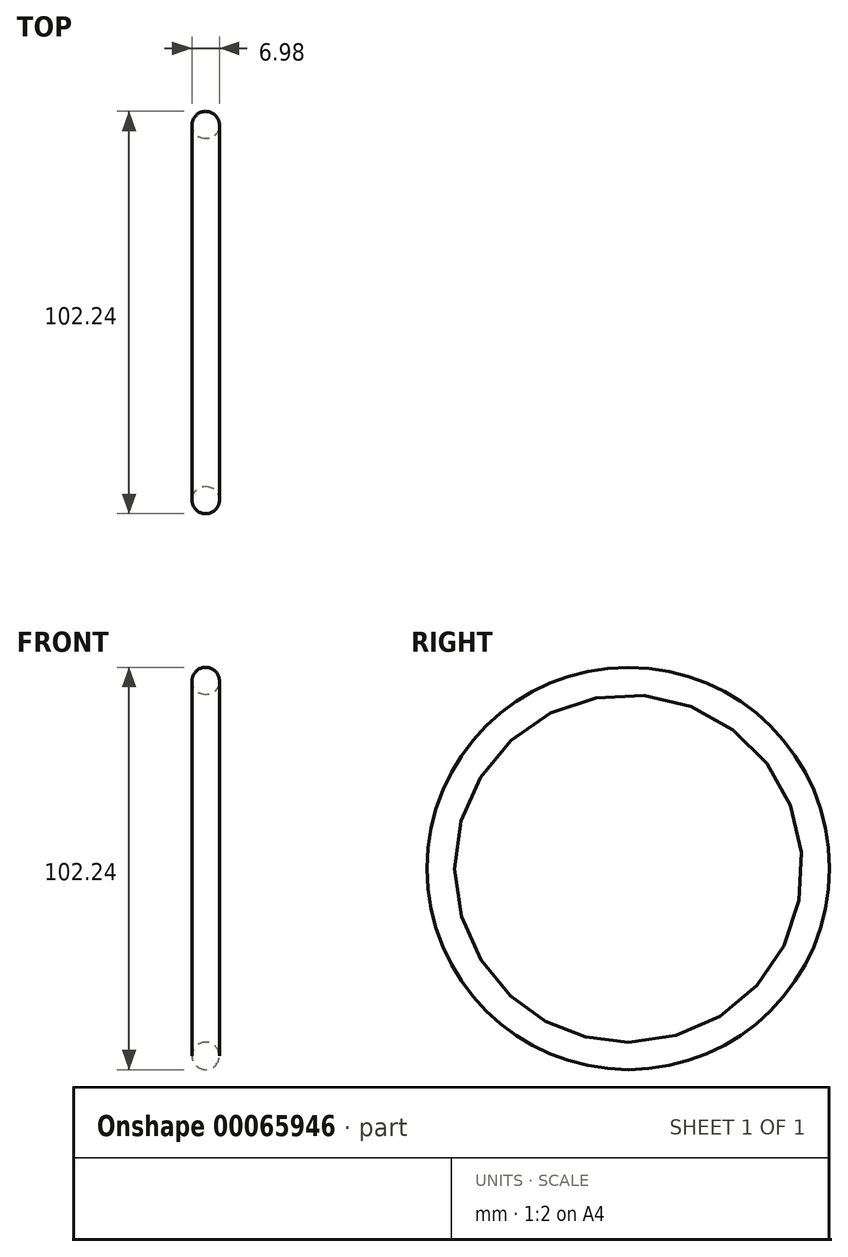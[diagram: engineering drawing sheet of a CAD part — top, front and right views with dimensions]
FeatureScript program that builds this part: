
annotation { "Feature Type Name" : "Feature", "Feature Type Description" : "" }
export const myFeature = defineFeature(function(context is Context, id is Id, definition is map)
    precondition{}
    {
        {
            var Q0;
            Q0=qCreatedBy(makeId("Front.planeOp"),FACE);
            var sketch = newSketch(context, id + "F0", { "sketchPlane" : qUnion([Q0])});
            skLineSegment(sketch, "E0", {"start": v(0, 0) * mm, "end": v(-6.06, 0) * mm, "construction": true});
            skCircle(sketch, "E1", {"center": v(0, 47.63) * mm, "radius": 3.5 * mm});
            skSolve(sketch);
        }
        {
            var Q0;
            Q0=makeQuery(id+"F0.imprint","IMPRINT",FACE,{"disambiguationData":[TD([[makeQuery(id+"F0.imprint","IMPRINT",EDGE,{"derivedFrom":sQuery(id+"F0.wireOp",EDGE,"E1")}),1.0]])]});
            var Q1;
            Q1=sQuery(id+"F0.wireOp",EDGE,"E0");
            revolve(context, id + "F1", {"entities" : qUnion([Q0]), "axis" : qUnion([Q1]), "revolveType" : RevolveType.FULL});
        }
    });
